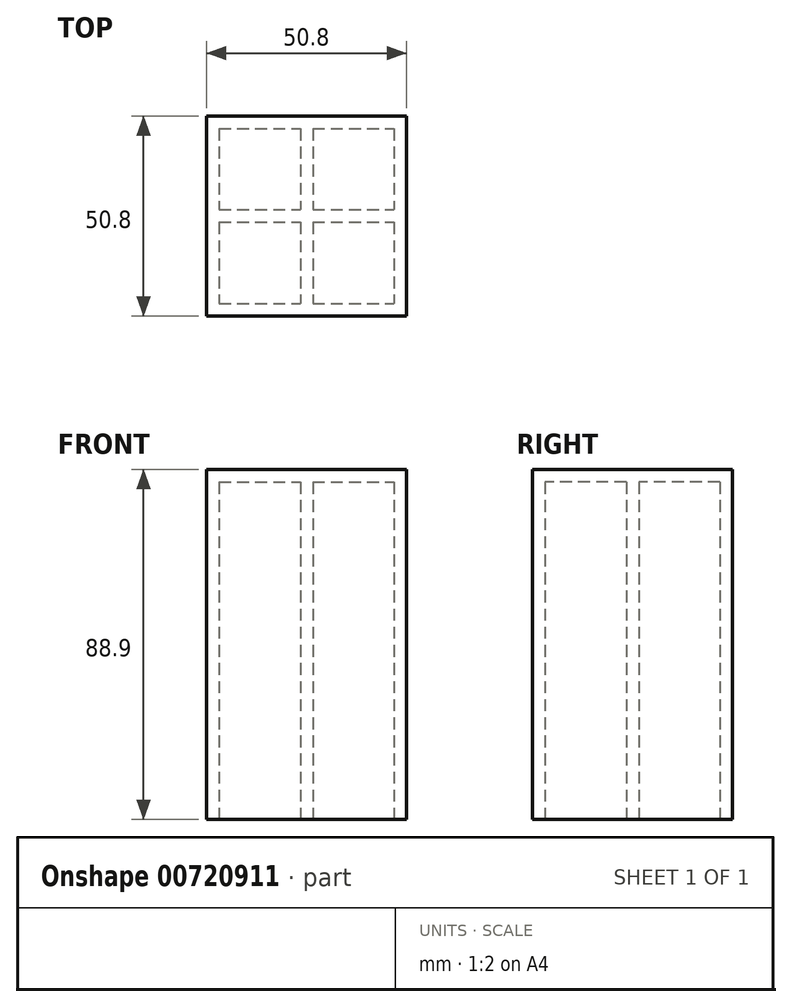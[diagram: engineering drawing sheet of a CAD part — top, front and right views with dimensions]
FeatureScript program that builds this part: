
annotation { "Feature Type Name" : "Feature", "Feature Type Description" : "" }
export const myFeature = defineFeature(function(context is Context, id is Id, definition is map)
    precondition{}
    {
        {
            var Q0;
            Q0=qCreatedBy(makeId("Top.planeOp"),FACE);
            var sketch = newSketch(context, id + "F0", { "sketchPlane" : qUnion([Q0])});
            skLineSegment(sketch, "E0.bottom", {"start": v(-50.8, 50.8) * mm, "end": v(0, 50.8) * mm});
            skLineSegment(sketch, "E0.top", {"start": v(-50.8, 0) * mm, "end": v(0, 0) * mm});
            skLineSegment(sketch, "E0.left", {"start": v(-50.8, 50.8) * mm, "end": v(-50.8, 0) * mm});
            skLineSegment(sketch, "E0.right", {"start": v(0, 50.8) * mm, "end": v(0, 0) * mm});
            skSolve(sketch);
        }
        {
            var Q0;
            Q0=makeQuery(id+"F0.imprint","IMPRINT",FACE,{"disambiguationData":[TD([[makeQuery(id+"F0.imprint","IMPRINT",EDGE,{"derivedFrom":sQuery(id+"F0.wireOp",EDGE,"E0.bottom")}),-1.0]])]});
            extrude(context, id + "F1", {"entities" : qUnion([Q0]), "depth" : 88.9 * mm, "offsetDistance" : 25.4 * mm});
        }
        {
            var Q0;
            Q0=qCreatedBy(makeId("Top.planeOp"),FACE);
            var sketch = newSketch(context, id + "F2", { "sketchPlane" : qUnion([Q0])});
            skLineSegment(sketch, "E1.bottom", {"start": v(-47.63, 47.63) * mm, "end": v(-26.99, 47.63) * mm});
            skLineSegment(sketch, "E1.top", {"start": v(-47.63, 26.99) * mm, "end": v(-26.99, 26.99) * mm});
            skLineSegment(sketch, "E1.left", {"start": v(-47.63, 47.63) * mm, "end": v(-47.63, 26.99) * mm});
            skLineSegment(sketch, "E1.right", {"start": v(-26.99, 47.63) * mm, "end": v(-26.99, 26.99) * mm});
            skLineSegment(sketch, "E2.bottom", {"start": v(-23.81, 47.62) * mm, "end": v(-3.18, 47.62) * mm});
            skLineSegment(sketch, "E2.top", {"start": v(-23.81, 26.99) * mm, "end": v(-3.18, 26.99) * mm});
            skLineSegment(sketch, "E2.left", {"start": v(-23.81, 47.62) * mm, "end": v(-23.81, 26.99) * mm});
            skLineSegment(sketch, "E2.right", {"start": v(-3.18, 47.62) * mm, "end": v(-3.18, 26.99) * mm});
            skLineSegment(sketch, "E3.bottom", {"start": v(-47.63, 23.81) * mm, "end": v(-26.99, 23.81) * mm});
            skLineSegment(sketch, "E3.top", {"start": v(-47.63, 3.18) * mm, "end": v(-26.99, 3.18) * mm});
            skLineSegment(sketch, "E3.left", {"start": v(-47.63, 23.81) * mm, "end": v(-47.63, 3.18) * mm});
            skLineSegment(sketch, "E3.right", {"start": v(-26.99, 23.81) * mm, "end": v(-26.99, 3.18) * mm});
            skLineSegment(sketch, "E4.bottom", {"start": v(-23.81, 23.81) * mm, "end": v(-3.18, 23.81) * mm});
            skLineSegment(sketch, "E4.top", {"start": v(-23.81, 3.18) * mm, "end": v(-3.18, 3.18) * mm});
            skLineSegment(sketch, "E4.left", {"start": v(-23.81, 23.81) * mm, "end": v(-23.81, 3.18) * mm});
            skLineSegment(sketch, "E4.right", {"start": v(-3.18, 23.81) * mm, "end": v(-3.18, 3.18) * mm});
            skSolve(sketch);
        }
        {
            var Q0;
            Q0 = qSketchRegion(id + "F2", true);
            extrude(context, id + "F3", {"entities" : qUnion([Q0]), "operationType" : NewBodyOperationType.REMOVE, "depth" : 85.72 * mm, "offsetDistance" : 25.4 * mm});
        }
    });
